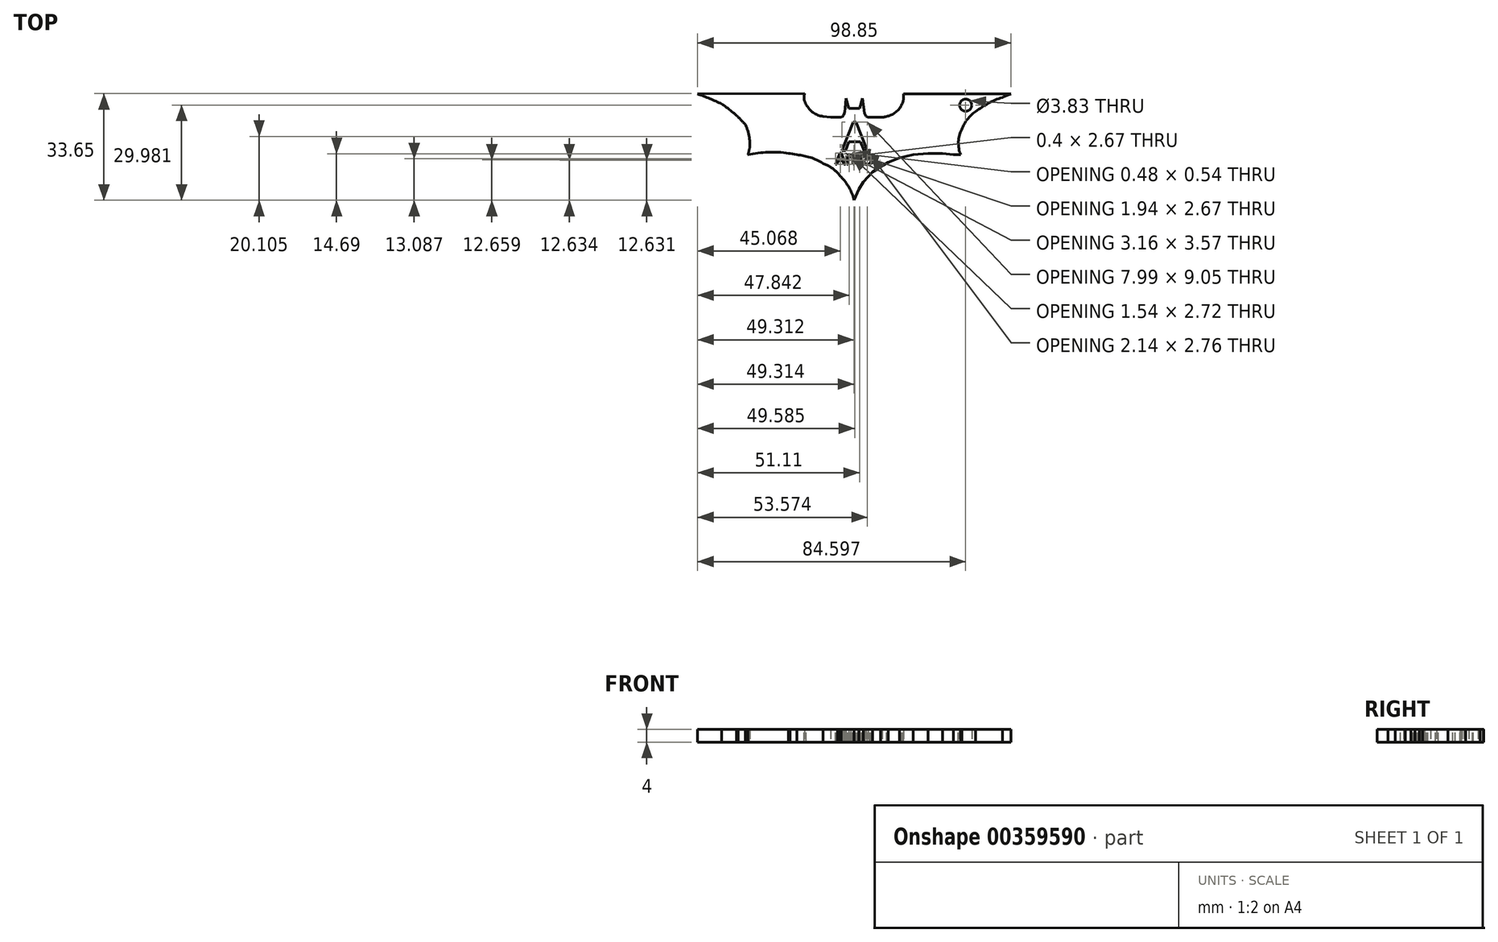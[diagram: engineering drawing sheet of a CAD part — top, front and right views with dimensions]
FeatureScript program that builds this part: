
annotation { "Feature Type Name" : "Feature", "Feature Type Description" : "" }
export const myFeature = defineFeature(function(context is Context, id is Id, definition is map)
    precondition{}
    {
        {
            var Q0;
            Q0=qCreatedBy(makeId("Top.planeOp"),FACE);
            var sketch = newSketch(context, id + "F0", { "sketchPlane" : qUnion([Q0])});
            skLineSegment(sketch, "E0", {"start": v(13.72, 31.25) * mm, "end": v(13.72, 28.83) * mm});
            skLineSegment(sketch, "E1", {"start": v(13.72, 28.83) * mm, "end": v(14.25, 27.77) * mm});
            skLineSegment(sketch, "E2", {"start": v(14.25, 27.77) * mm, "end": v(14.95, 26.82) * mm});
            skLineSegment(sketch, "E3", {"start": v(14.95, 26.82) * mm, "end": v(16.13, 25.57) * mm});
            skLineSegment(sketch, "E4", {"start": v(16.13, 25.57) * mm, "end": v(17.63, 24.91) * mm});
            skLineSegment(sketch, "E5", {"start": v(17.63, 24.91) * mm, "end": v(18.98, 24.45) * mm});
            skLineSegment(sketch, "E6", {"start": v(18.98, 24.45) * mm, "end": v(20.46, 24) * mm});
            skLineSegment(sketch, "E7", {"start": v(20.46, 24) * mm, "end": v(21.96, 23.73) * mm});
            skLineSegment(sketch, "E8", {"start": v(21.96, 23.73) * mm, "end": v(23.63, 23.73) * mm});
            skLineSegment(sketch, "E9", {"start": v(23.63, 23.73) * mm, "end": v(24.39, 23.73) * mm});
            skLineSegment(sketch, "E10", {"start": v(24.39, 23.73) * mm, "end": v(25.19, 23.73) * mm});
            skLineSegment(sketch, "E11", {"start": v(25.19, 23.73) * mm, "end": v(25.75, 24) * mm});
            skLineSegment(sketch, "E12", {"start": v(25.75, 24) * mm, "end": v(26, 24.45) * mm});
            skLineSegment(sketch, "E13", {"start": v(26, 24.45) * mm, "end": v(26.24, 25.03) * mm});
            skLineSegment(sketch, "E14", {"start": v(26.24, 25.03) * mm, "end": v(26.34, 25.57) * mm});
            skLineSegment(sketch, "E15", {"start": v(26.34, 25.57) * mm, "end": v(26.47, 26.55) * mm});
            skLineSegment(sketch, "E16", {"start": v(26.47, 26.55) * mm, "end": v(26.64, 28.28) * mm});
            skLineSegment(sketch, "E17", {"start": v(26.64, 28.28) * mm, "end": v(26.78, 29.75) * mm});
            skLineSegment(sketch, "E18", {"start": v(26.78, 29.75) * mm, "end": v(27.66, 26.55) * mm});
            skLineSegment(sketch, "E19", {"start": v(27.66, 26.55) * mm, "end": v(29.82, 26.55) * mm});
            skLineSegment(sketch, "E20", {"start": v(29.82, 26.55) * mm, "end": v(31.09, 26.55) * mm});
            skLineSegment(sketch, "E21", {"start": v(31.09, 26.55) * mm, "end": v(32.02, 29.75) * mm});
            skLineSegment(sketch, "E22", {"start": v(32.02, 29.75) * mm, "end": v(32.64, 25.03) * mm});
            skLineSegment(sketch, "E23", {"start": v(32.64, 25.03) * mm, "end": v(33.17, 24) * mm});
            skLineSegment(sketch, "E24", {"start": v(33.17, 24) * mm, "end": v(33.75, 23.73) * mm});
            skLineSegment(sketch, "E25", {"start": v(33.75, 23.73) * mm, "end": v(35.1, 23.73) * mm});
            skLineSegment(sketch, "E26", {"start": v(35.1, 23.73) * mm, "end": v(36.67, 23.73) * mm});
            skLineSegment(sketch, "E27", {"start": v(36.67, 23.73) * mm, "end": v(38.2, 23.73) * mm});
            skLineSegment(sketch, "E28", {"start": v(38.2, 23.73) * mm, "end": v(39.59, 24) * mm});
            skLineSegment(sketch, "E29", {"start": v(39.59, 24) * mm, "end": v(41.11, 25.03) * mm});
            skLineSegment(sketch, "E30", {"start": v(41.11, 25.03) * mm, "end": v(42.73, 25.57) * mm});
            skLineSegment(sketch, "E31", {"start": v(42.73, 25.57) * mm, "end": v(43.58, 26.55) * mm});
            skLineSegment(sketch, "E32", {"start": v(43.58, 26.55) * mm, "end": v(44.48, 27.96) * mm});
            skLineSegment(sketch, "E33", {"start": v(44.48, 27.96) * mm, "end": v(44.93, 29.4) * mm});
            skLineSegment(sketch, "E34", {"start": v(44.93, 29.4) * mm, "end": v(44.93, 31.1) * mm});
            skLineSegment(sketch, "E35", {"start": v(44.93, 31.1) * mm, "end": v(78.8, 31.1) * mm});
            skLineSegment(sketch, "E36", {"start": v(78.8, 31.1) * mm, "end": v(73.5, 29.03) * mm});
            skLineSegment(sketch, "E37", {"start": v(73.5, 29.03) * mm, "end": v(70.71, 27.5) * mm});
            skLineSegment(sketch, "E38", {"start": v(70.71, 27.5) * mm, "end": v(67.7, 25.57) * mm});
            skLineSegment(sketch, "E39", {"start": v(67.7, 25.57) * mm, "end": v(65.18, 22.94) * mm});
            skLineSegment(sketch, "E40", {"start": v(65.18, 22.94) * mm, "end": v(64.06, 21.44) * mm});
            skLineSegment(sketch, "E41", {"start": v(64.06, 21.44) * mm, "end": v(63.33, 19.97) * mm});
            skLineSegment(sketch, "E42", {"start": v(63.33, 19.97) * mm, "end": v(62.51, 17.77) * mm});
            skLineSegment(sketch, "E43", {"start": v(62.51, 17.77) * mm, "end": v(62.51, 15.4) * mm});
            skLineSegment(sketch, "E44", {"start": v(62.51, 15.4) * mm, "end": v(63, 11.92) * mm});
            skLineSegment(sketch, "E45", {"start": v(63, 11.92) * mm, "end": v(60.67, 11.92) * mm});
            skLineSegment(sketch, "E46", {"start": v(60.67, 11.92) * mm, "end": v(57.24, 12.33) * mm});
            skLineSegment(sketch, "E47", {"start": v(57.24, 12.33) * mm, "end": v(52.7, 12.33) * mm});
            skLineSegment(sketch, "E48", {"start": v(52.7, 12.33) * mm, "end": v(48.05, 11.92) * mm});
            skLineSegment(sketch, "E49", {"start": v(48.05, 11.92) * mm, "end": v(43.68, 10.94) * mm});
            skLineSegment(sketch, "E50", {"start": v(43.68, 10.94) * mm, "end": v(40.1, 9.5) * mm});
            skLineSegment(sketch, "E51", {"start": v(40.1, 9.5) * mm, "end": v(37.65, 8.21) * mm});
            skLineSegment(sketch, "E52", {"start": v(37.65, 8.21) * mm, "end": v(35.1, 6.52) * mm});
            skLineSegment(sketch, "E53", {"start": v(35.1, 6.52) * mm, "end": v(32.18, 3.37) * mm});
            skLineSegment(sketch, "E54", {"start": v(32.18, 3.37) * mm, "end": v(30.81, 1.1) * mm});
            skLineSegment(sketch, "E55", {"start": v(30.81, 1.1) * mm, "end": v(29.34, -2.4) * mm});
            skLineSegment(sketch, "E56", {"start": v(29.34, -2.4) * mm, "end": v(27.5, 2) * mm});
            skLineSegment(sketch, "E57", {"start": v(27.5, 2) * mm, "end": v(26, 3.93) * mm});
            skLineSegment(sketch, "E58", {"start": v(26, 3.93) * mm, "end": v(24.39, 6.05) * mm});
            skLineSegment(sketch, "E59", {"start": v(24.39, 6.05) * mm, "end": v(22.41, 7.44) * mm});
            skLineSegment(sketch, "E60", {"start": v(22.41, 7.44) * mm, "end": v(20.46, 8.75) * mm});
            skLineSegment(sketch, "E61", {"start": v(20.46, 8.75) * mm, "end": v(17.41, 10.24) * mm});
            skLineSegment(sketch, "E62", {"start": v(17.41, 10.24) * mm, "end": v(14.24, 11.29) * mm});
            skLineSegment(sketch, "E63", {"start": v(14.24, 11.29) * mm, "end": v(11.29, 11.92) * mm});
            skLineSegment(sketch, "E64", {"start": v(11.29, 11.92) * mm, "end": v(9.12, 12.4) * mm});
            skLineSegment(sketch, "E65", {"start": v(9.12, 12.4) * mm, "end": v(5.3, 12.4) * mm});
            skLineSegment(sketch, "E66", {"start": v(5.3, 12.4) * mm, "end": v(2.38, 12.4) * mm});
            skLineSegment(sketch, "E67", {"start": v(2.38, 12.4) * mm, "end": v(-0.95, 12.4) * mm});
            skLineSegment(sketch, "E68", {"start": v(-0.95, 12.4) * mm, "end": v(-4.16, 11.92) * mm});
            skLineSegment(sketch, "E69", {"start": v(-4.16, 11.92) * mm, "end": v(-3.57, 14.45) * mm});
            skLineSegment(sketch, "E70", {"start": v(-3.57, 14.45) * mm, "end": v(-3.57, 16.43) * mm});
            skLineSegment(sketch, "E71", {"start": v(-3.57, 16.43) * mm, "end": v(-4.05, 19) * mm});
            skLineSegment(sketch, "E72", {"start": v(-4.05, 19) * mm, "end": v(-5, 21.44) * mm});
            skLineSegment(sketch, "E73", {"start": v(-5, 21.44) * mm, "end": v(-6.4, 22.94) * mm});
            skLineSegment(sketch, "E74", {"start": v(-6.4, 22.94) * mm, "end": v(-7.45, 24) * mm});
            skLineSegment(sketch, "E75", {"start": v(-7.45, 24) * mm, "end": v(-9.22, 25.57) * mm});
            skLineSegment(sketch, "E76", {"start": v(-9.22, 25.57) * mm, "end": v(-10.64, 26.55) * mm});
            skLineSegment(sketch, "E77", {"start": v(-10.64, 26.55) * mm, "end": v(-12.42, 27.96) * mm});
            skLineSegment(sketch, "E78", {"start": v(-12.42, 27.96) * mm, "end": v(-15.57, 29.4) * mm});
            skLineSegment(sketch, "E79", {"start": v(-15.57, 29.4) * mm, "end": v(-20.04, 31.1) * mm});
            skLineSegment(sketch, "E80", {"start": v(-20.04, 31.1) * mm, "end": v(13.72, 31.25) * mm});
            skSolve(sketch);
        }
        {
            var Q0;
            Q0 = qSketchRegion(id + "F0", true);
            extrude(context, id + "F1", {"entities" : qUnion([Q0]), "depth" : 4 * mm});
        }
        {
            var Q0;
            Q0=makeQuery(id+"F1.opExtrude","CAP_FACE",FACE,{"disambiguationData":[OSD([sQuery(id+"F0.wireOp",EDGE,"E0"),sQuery(id+"F0.wireOp",EDGE,"E1"),sQuery(id+"F0.wireOp",EDGE,"E2"),sQuery(id+"F0.wireOp",EDGE,"E3"),sQuery(id+"F0.wireOp",EDGE,"E4"),sQuery(id+"F0.wireOp",EDGE,"E5"),sQuery(id+"F0.wireOp",EDGE,"E6"),sQuery(id+"F0.wireOp",EDGE,"E7"),sQuery(id+"F0.wireOp",EDGE,"E8"),sQuery(id+"F0.wireOp",EDGE,"E9"),sQuery(id+"F0.wireOp",EDGE,"E10"),sQuery(id+"F0.wireOp",EDGE,"E11"),sQuery(id+"F0.wireOp",EDGE,"E12"),sQuery(id+"F0.wireOp",EDGE,"E13"),sQuery(id+"F0.wireOp",EDGE,"E14"),sQuery(id+"F0.wireOp",EDGE,"E15"),sQuery(id+"F0.wireOp",EDGE,"E16"),sQuery(id+"F0.wireOp",EDGE,"E17"),sQuery(id+"F0.wireOp",EDGE,"E18"),sQuery(id+"F0.wireOp",EDGE,"E19"),sQuery(id+"F0.wireOp",EDGE,"E20"),sQuery(id+"F0.wireOp",EDGE,"E21"),sQuery(id+"F0.wireOp",EDGE,"E22"),sQuery(id+"F0.wireOp",EDGE,"E23"),sQuery(id+"F0.wireOp",EDGE,"E24"),sQuery(id+"F0.wireOp",EDGE,"E25"),sQuery(id+"F0.wireOp",EDGE,"E26"),sQuery(id+"F0.wireOp",EDGE,"E27"),sQuery(id+"F0.wireOp",EDGE,"E28"),sQuery(id+"F0.wireOp",EDGE,"E29"),sQuery(id+"F0.wireOp",EDGE,"E30"),sQuery(id+"F0.wireOp",EDGE,"E31"),sQuery(id+"F0.wireOp",EDGE,"E32"),sQuery(id+"F0.wireOp",EDGE,"E33"),sQuery(id+"F0.wireOp",EDGE,"E34"),sQuery(id+"F0.wireOp",EDGE,"E35"),sQuery(id+"F0.wireOp",EDGE,"E36"),sQuery(id+"F0.wireOp",EDGE,"E37"),sQuery(id+"F0.wireOp",EDGE,"E38"),sQuery(id+"F0.wireOp",EDGE,"E39"),sQuery(id+"F0.wireOp",EDGE,"E40"),sQuery(id+"F0.wireOp",EDGE,"E41"),sQuery(id+"F0.wireOp",EDGE,"E42"),sQuery(id+"F0.wireOp",EDGE,"E43"),sQuery(id+"F0.wireOp",EDGE,"E44"),sQuery(id+"F0.wireOp",EDGE,"E45"),sQuery(id+"F0.wireOp",EDGE,"E46"),sQuery(id+"F0.wireOp",EDGE,"E47"),sQuery(id+"F0.wireOp",EDGE,"E48"),sQuery(id+"F0.wireOp",EDGE,"E49"),sQuery(id+"F0.wireOp",EDGE,"E50"),sQuery(id+"F0.wireOp",EDGE,"E51"),sQuery(id+"F0.wireOp",EDGE,"E52"),sQuery(id+"F0.wireOp",EDGE,"E53"),sQuery(id+"F0.wireOp",EDGE,"E54"),sQuery(id+"F0.wireOp",EDGE,"E55"),sQuery(id+"F0.wireOp",EDGE,"E56"),sQuery(id+"F0.wireOp",EDGE,"E57"),sQuery(id+"F0.wireOp",EDGE,"E58"),sQuery(id+"F0.wireOp",EDGE,"E59"),sQuery(id+"F0.wireOp",EDGE,"E60"),sQuery(id+"F0.wireOp",EDGE,"E61"),sQuery(id+"F0.wireOp",EDGE,"E62"),sQuery(id+"F0.wireOp",EDGE,"E63"),sQuery(id+"F0.wireOp",EDGE,"E64"),sQuery(id+"F0.wireOp",EDGE,"E65"),sQuery(id+"F0.wireOp",EDGE,"E66"),sQuery(id+"F0.wireOp",EDGE,"E67"),sQuery(id+"F0.wireOp",EDGE,"E68"),sQuery(id+"F0.wireOp",EDGE,"E69"),sQuery(id+"F0.wireOp",EDGE,"E70"),sQuery(id+"F0.wireOp",EDGE,"E71"),sQuery(id+"F0.wireOp",EDGE,"E72"),sQuery(id+"F0.wireOp",EDGE,"E73"),sQuery(id+"F0.wireOp",EDGE,"E74"),sQuery(id+"F0.wireOp",EDGE,"E75"),sQuery(id+"F0.wireOp",EDGE,"E76"),sQuery(id+"F0.wireOp",EDGE,"E77"),sQuery(id+"F0.wireOp",EDGE,"E78"),sQuery(id+"F0.wireOp",EDGE,"E79"),sQuery(id+"F0.wireOp",EDGE,"E80")])],"isStart":false});
            var sketch = newSketch(context, id + "F2", { "sketchPlane" : qUnion([Q0])});
            skArc(sketch, "E81", {"start": v(44.48, 27.96) * mm, "mid": v(44.94, 29.5) * mm, "end": v(44.93, 31.1) * mm});
            skArc(sketch, "E82", {"start": v(39.59, 24) * mm, "mid": v(42.52, 25.38) * mm, "end": v(44.48, 27.96) * mm});
            skArc(sketch, "E83", {"start": v(38.2, 23.73) * mm, "mid": v(38.9, 23.86) * mm, "end": v(39.59, 24) * mm});
            skLineSegment(sketch, "E84", {"start": v(38.2, 23.73) * mm, "end": v(44.93, 31.1) * mm});
            skSolve(sketch);
        }
        {
            var Q0;
            Q0 = qSketchRegion(id + "F2", true);
            extrude(context, id + "F3", {"entities" : qUnion([Q0]), "operationType" : NewBodyOperationType.REMOVE, "oppositeDirection" : true, "depth" : 25 * mm});
        }
        {
            var Q0;
            Q0=makeQuery(id+"F1.opExtrude","CAP_FACE",FACE,{"disambiguationData":[OSD([sQuery(id+"F0.wireOp",EDGE,"E0"),sQuery(id+"F0.wireOp",EDGE,"E1"),sQuery(id+"F0.wireOp",EDGE,"E2"),sQuery(id+"F0.wireOp",EDGE,"E3"),sQuery(id+"F0.wireOp",EDGE,"E4"),sQuery(id+"F0.wireOp",EDGE,"E5"),sQuery(id+"F0.wireOp",EDGE,"E6"),sQuery(id+"F0.wireOp",EDGE,"E7"),sQuery(id+"F0.wireOp",EDGE,"E8"),sQuery(id+"F0.wireOp",EDGE,"E9"),sQuery(id+"F0.wireOp",EDGE,"E10"),sQuery(id+"F0.wireOp",EDGE,"E11"),sQuery(id+"F0.wireOp",EDGE,"E12"),sQuery(id+"F0.wireOp",EDGE,"E13"),sQuery(id+"F0.wireOp",EDGE,"E14"),sQuery(id+"F0.wireOp",EDGE,"E15"),sQuery(id+"F0.wireOp",EDGE,"E16"),sQuery(id+"F0.wireOp",EDGE,"E17"),sQuery(id+"F0.wireOp",EDGE,"E18"),sQuery(id+"F0.wireOp",EDGE,"E19"),sQuery(id+"F0.wireOp",EDGE,"E20"),sQuery(id+"F0.wireOp",EDGE,"E21"),sQuery(id+"F0.wireOp",EDGE,"E22"),sQuery(id+"F0.wireOp",EDGE,"E23"),sQuery(id+"F0.wireOp",EDGE,"E24"),sQuery(id+"F0.wireOp",EDGE,"E25"),sQuery(id+"F0.wireOp",EDGE,"E26"),sQuery(id+"F0.wireOp",EDGE,"E27"),sQuery(id+"F0.wireOp",EDGE,"E28"),sQuery(id+"F0.wireOp",EDGE,"E29"),sQuery(id+"F0.wireOp",EDGE,"E30"),sQuery(id+"F0.wireOp",EDGE,"E31"),sQuery(id+"F0.wireOp",EDGE,"E32"),sQuery(id+"F0.wireOp",EDGE,"E33"),sQuery(id+"F0.wireOp",EDGE,"E34"),sQuery(id+"F0.wireOp",EDGE,"E35"),sQuery(id+"F0.wireOp",EDGE,"E36"),sQuery(id+"F0.wireOp",EDGE,"E37"),sQuery(id+"F0.wireOp",EDGE,"E38"),sQuery(id+"F0.wireOp",EDGE,"E39"),sQuery(id+"F0.wireOp",EDGE,"E40"),sQuery(id+"F0.wireOp",EDGE,"E41"),sQuery(id+"F0.wireOp",EDGE,"E42"),sQuery(id+"F0.wireOp",EDGE,"E43"),sQuery(id+"F0.wireOp",EDGE,"E44"),sQuery(id+"F0.wireOp",EDGE,"E45"),sQuery(id+"F0.wireOp",EDGE,"E46"),sQuery(id+"F0.wireOp",EDGE,"E47"),sQuery(id+"F0.wireOp",EDGE,"E48"),sQuery(id+"F0.wireOp",EDGE,"E49"),sQuery(id+"F0.wireOp",EDGE,"E50"),sQuery(id+"F0.wireOp",EDGE,"E51"),sQuery(id+"F0.wireOp",EDGE,"E52"),sQuery(id+"F0.wireOp",EDGE,"E53"),sQuery(id+"F0.wireOp",EDGE,"E54"),sQuery(id+"F0.wireOp",EDGE,"E55"),sQuery(id+"F0.wireOp",EDGE,"E56"),sQuery(id+"F0.wireOp",EDGE,"E57"),sQuery(id+"F0.wireOp",EDGE,"E58"),sQuery(id+"F0.wireOp",EDGE,"E59"),sQuery(id+"F0.wireOp",EDGE,"E60"),sQuery(id+"F0.wireOp",EDGE,"E61"),sQuery(id+"F0.wireOp",EDGE,"E62"),sQuery(id+"F0.wireOp",EDGE,"E63"),sQuery(id+"F0.wireOp",EDGE,"E64"),sQuery(id+"F0.wireOp",EDGE,"E65"),sQuery(id+"F0.wireOp",EDGE,"E66"),sQuery(id+"F0.wireOp",EDGE,"E67"),sQuery(id+"F0.wireOp",EDGE,"E68"),sQuery(id+"F0.wireOp",EDGE,"E69"),sQuery(id+"F0.wireOp",EDGE,"E70"),sQuery(id+"F0.wireOp",EDGE,"E71"),sQuery(id+"F0.wireOp",EDGE,"E72"),sQuery(id+"F0.wireOp",EDGE,"E73"),sQuery(id+"F0.wireOp",EDGE,"E74"),sQuery(id+"F0.wireOp",EDGE,"E75"),sQuery(id+"F0.wireOp",EDGE,"E76"),sQuery(id+"F0.wireOp",EDGE,"E77"),sQuery(id+"F0.wireOp",EDGE,"E78"),sQuery(id+"F0.wireOp",EDGE,"E79"),sQuery(id+"F0.wireOp",EDGE,"E80")])],"isStart":false});
            var sketch = newSketch(context, id + "F4", { "sketchPlane" : qUnion([Q0])});
            skArc(sketch, "E85", {"start": v(13.72, 31.25) * mm, "mid": v(13.57, 29.44) * mm, "end": v(14.25, 27.77) * mm});
            skArc(sketch, "E86", {"start": v(14.25, 27.77) * mm, "mid": v(16.81, 24.99) * mm, "end": v(20.46, 24) * mm});
            skLineSegment(sketch, "E87", {"start": v(20.46, 24) * mm, "end": v(13.72, 31.25) * mm});
            skSolve(sketch);
        }
        {
            var Q0;
            Q0 = qSketchRegion(id + "F4", true);
            extrude(context, id + "F5", {"entities" : qUnion([Q0]), "operationType" : NewBodyOperationType.REMOVE, "oppositeDirection" : true, "depth" : 25 * mm});
        }
        {
            var Q0;
            Q0=makeQuery(id+"F1.opExtrude","CAP_FACE",FACE,{"disambiguationData":[OSD([sQuery(id+"F0.wireOp",EDGE,"E0"),sQuery(id+"F0.wireOp",EDGE,"E1"),sQuery(id+"F0.wireOp",EDGE,"E2"),sQuery(id+"F0.wireOp",EDGE,"E3"),sQuery(id+"F0.wireOp",EDGE,"E4"),sQuery(id+"F0.wireOp",EDGE,"E5"),sQuery(id+"F0.wireOp",EDGE,"E6"),sQuery(id+"F0.wireOp",EDGE,"E7"),sQuery(id+"F0.wireOp",EDGE,"E8"),sQuery(id+"F0.wireOp",EDGE,"E9"),sQuery(id+"F0.wireOp",EDGE,"E10"),sQuery(id+"F0.wireOp",EDGE,"E11"),sQuery(id+"F0.wireOp",EDGE,"E12"),sQuery(id+"F0.wireOp",EDGE,"E13"),sQuery(id+"F0.wireOp",EDGE,"E14"),sQuery(id+"F0.wireOp",EDGE,"E15"),sQuery(id+"F0.wireOp",EDGE,"E16"),sQuery(id+"F0.wireOp",EDGE,"E17"),sQuery(id+"F0.wireOp",EDGE,"E18"),sQuery(id+"F0.wireOp",EDGE,"E19"),sQuery(id+"F0.wireOp",EDGE,"E20"),sQuery(id+"F0.wireOp",EDGE,"E21"),sQuery(id+"F0.wireOp",EDGE,"E22"),sQuery(id+"F0.wireOp",EDGE,"E23"),sQuery(id+"F0.wireOp",EDGE,"E24"),sQuery(id+"F0.wireOp",EDGE,"E25"),sQuery(id+"F0.wireOp",EDGE,"E26"),sQuery(id+"F0.wireOp",EDGE,"E27"),sQuery(id+"F0.wireOp",EDGE,"E28"),sQuery(id+"F0.wireOp",EDGE,"E29"),sQuery(id+"F0.wireOp",EDGE,"E30"),sQuery(id+"F0.wireOp",EDGE,"E31"),sQuery(id+"F0.wireOp",EDGE,"E32"),sQuery(id+"F0.wireOp",EDGE,"E33"),sQuery(id+"F0.wireOp",EDGE,"E34"),sQuery(id+"F0.wireOp",EDGE,"E35"),sQuery(id+"F0.wireOp",EDGE,"E36"),sQuery(id+"F0.wireOp",EDGE,"E37"),sQuery(id+"F0.wireOp",EDGE,"E38"),sQuery(id+"F0.wireOp",EDGE,"E39"),sQuery(id+"F0.wireOp",EDGE,"E40"),sQuery(id+"F0.wireOp",EDGE,"E41"),sQuery(id+"F0.wireOp",EDGE,"E42"),sQuery(id+"F0.wireOp",EDGE,"E43"),sQuery(id+"F0.wireOp",EDGE,"E44"),sQuery(id+"F0.wireOp",EDGE,"E45"),sQuery(id+"F0.wireOp",EDGE,"E46"),sQuery(id+"F0.wireOp",EDGE,"E47"),sQuery(id+"F0.wireOp",EDGE,"E48"),sQuery(id+"F0.wireOp",EDGE,"E49"),sQuery(id+"F0.wireOp",EDGE,"E50"),sQuery(id+"F0.wireOp",EDGE,"E51"),sQuery(id+"F0.wireOp",EDGE,"E52"),sQuery(id+"F0.wireOp",EDGE,"E53"),sQuery(id+"F0.wireOp",EDGE,"E54"),sQuery(id+"F0.wireOp",EDGE,"E55"),sQuery(id+"F0.wireOp",EDGE,"E56"),sQuery(id+"F0.wireOp",EDGE,"E57"),sQuery(id+"F0.wireOp",EDGE,"E58"),sQuery(id+"F0.wireOp",EDGE,"E59"),sQuery(id+"F0.wireOp",EDGE,"E60"),sQuery(id+"F0.wireOp",EDGE,"E61"),sQuery(id+"F0.wireOp",EDGE,"E62"),sQuery(id+"F0.wireOp",EDGE,"E63"),sQuery(id+"F0.wireOp",EDGE,"E64"),sQuery(id+"F0.wireOp",EDGE,"E65"),sQuery(id+"F0.wireOp",EDGE,"E66"),sQuery(id+"F0.wireOp",EDGE,"E67"),sQuery(id+"F0.wireOp",EDGE,"E68"),sQuery(id+"F0.wireOp",EDGE,"E69"),sQuery(id+"F0.wireOp",EDGE,"E70"),sQuery(id+"F0.wireOp",EDGE,"E71"),sQuery(id+"F0.wireOp",EDGE,"E72"),sQuery(id+"F0.wireOp",EDGE,"E73"),sQuery(id+"F0.wireOp",EDGE,"E74"),sQuery(id+"F0.wireOp",EDGE,"E75"),sQuery(id+"F0.wireOp",EDGE,"E76"),sQuery(id+"F0.wireOp",EDGE,"E77"),sQuery(id+"F0.wireOp",EDGE,"E78"),sQuery(id+"F0.wireOp",EDGE,"E79"),sQuery(id+"F0.wireOp",EDGE,"E80")])],"isStart":false});
            var sketch = newSketch(context, id + "F6", { "sketchPlane" : qUnion([Q0])});
            skLineSegment(sketch, "E88", {"start": v(19.36, 24.08) * mm, "end": v(21.96, 23.73) * mm});
            skLineSegment(sketch, "E89", {"start": v(21.96, 23.73) * mm, "end": v(21.96, 24.89) * mm});
            skLineSegment(sketch, "E90", {"start": v(21.96, 24.89) * mm, "end": v(19.54, 24.89) * mm});
            skLineSegment(sketch, "E91", {"start": v(19.54, 24.89) * mm, "end": v(19.36, 24.08) * mm});
            skSolve(sketch);
        }
        {
            var Q0;
            Q0 = qSketchRegion(id + "F6", true);
            extrude(context, id + "F7", {"entities" : qUnion([Q0]), "operationType" : NewBodyOperationType.REMOVE, "oppositeDirection" : true, "depth" : 25 * mm});
        }
        {
            var Q0;
            Q0=makeQuery(id+"F1.opExtrude","CAP_FACE",FACE,{"disambiguationData":[OSD([sQuery(id+"F0.wireOp",EDGE,"E0"),sQuery(id+"F0.wireOp",EDGE,"E1"),sQuery(id+"F0.wireOp",EDGE,"E2"),sQuery(id+"F0.wireOp",EDGE,"E3"),sQuery(id+"F0.wireOp",EDGE,"E4"),sQuery(id+"F0.wireOp",EDGE,"E5"),sQuery(id+"F0.wireOp",EDGE,"E6"),sQuery(id+"F0.wireOp",EDGE,"E7"),sQuery(id+"F0.wireOp",EDGE,"E8"),sQuery(id+"F0.wireOp",EDGE,"E9"),sQuery(id+"F0.wireOp",EDGE,"E10"),sQuery(id+"F0.wireOp",EDGE,"E11"),sQuery(id+"F0.wireOp",EDGE,"E12"),sQuery(id+"F0.wireOp",EDGE,"E13"),sQuery(id+"F0.wireOp",EDGE,"E14"),sQuery(id+"F0.wireOp",EDGE,"E15"),sQuery(id+"F0.wireOp",EDGE,"E16"),sQuery(id+"F0.wireOp",EDGE,"E17"),sQuery(id+"F0.wireOp",EDGE,"E18"),sQuery(id+"F0.wireOp",EDGE,"E19"),sQuery(id+"F0.wireOp",EDGE,"E20"),sQuery(id+"F0.wireOp",EDGE,"E21"),sQuery(id+"F0.wireOp",EDGE,"E22"),sQuery(id+"F0.wireOp",EDGE,"E23"),sQuery(id+"F0.wireOp",EDGE,"E24"),sQuery(id+"F0.wireOp",EDGE,"E25"),sQuery(id+"F0.wireOp",EDGE,"E26"),sQuery(id+"F0.wireOp",EDGE,"E27"),sQuery(id+"F0.wireOp",EDGE,"E28"),sQuery(id+"F0.wireOp",EDGE,"E29"),sQuery(id+"F0.wireOp",EDGE,"E30"),sQuery(id+"F0.wireOp",EDGE,"E31"),sQuery(id+"F0.wireOp",EDGE,"E32"),sQuery(id+"F0.wireOp",EDGE,"E33"),sQuery(id+"F0.wireOp",EDGE,"E34"),sQuery(id+"F0.wireOp",EDGE,"E35"),sQuery(id+"F0.wireOp",EDGE,"E36"),sQuery(id+"F0.wireOp",EDGE,"E37"),sQuery(id+"F0.wireOp",EDGE,"E38"),sQuery(id+"F0.wireOp",EDGE,"E39"),sQuery(id+"F0.wireOp",EDGE,"E40"),sQuery(id+"F0.wireOp",EDGE,"E41"),sQuery(id+"F0.wireOp",EDGE,"E42"),sQuery(id+"F0.wireOp",EDGE,"E43"),sQuery(id+"F0.wireOp",EDGE,"E44"),sQuery(id+"F0.wireOp",EDGE,"E45"),sQuery(id+"F0.wireOp",EDGE,"E46"),sQuery(id+"F0.wireOp",EDGE,"E47"),sQuery(id+"F0.wireOp",EDGE,"E48"),sQuery(id+"F0.wireOp",EDGE,"E49"),sQuery(id+"F0.wireOp",EDGE,"E50"),sQuery(id+"F0.wireOp",EDGE,"E51"),sQuery(id+"F0.wireOp",EDGE,"E52"),sQuery(id+"F0.wireOp",EDGE,"E53"),sQuery(id+"F0.wireOp",EDGE,"E54"),sQuery(id+"F0.wireOp",EDGE,"E55"),sQuery(id+"F0.wireOp",EDGE,"E56"),sQuery(id+"F0.wireOp",EDGE,"E57"),sQuery(id+"F0.wireOp",EDGE,"E58"),sQuery(id+"F0.wireOp",EDGE,"E59"),sQuery(id+"F0.wireOp",EDGE,"E60"),sQuery(id+"F0.wireOp",EDGE,"E61"),sQuery(id+"F0.wireOp",EDGE,"E62"),sQuery(id+"F0.wireOp",EDGE,"E63"),sQuery(id+"F0.wireOp",EDGE,"E64"),sQuery(id+"F0.wireOp",EDGE,"E65"),sQuery(id+"F0.wireOp",EDGE,"E66"),sQuery(id+"F0.wireOp",EDGE,"E67"),sQuery(id+"F0.wireOp",EDGE,"E68"),sQuery(id+"F0.wireOp",EDGE,"E69"),sQuery(id+"F0.wireOp",EDGE,"E70"),sQuery(id+"F0.wireOp",EDGE,"E71"),sQuery(id+"F0.wireOp",EDGE,"E72"),sQuery(id+"F0.wireOp",EDGE,"E73"),sQuery(id+"F0.wireOp",EDGE,"E74"),sQuery(id+"F0.wireOp",EDGE,"E75"),sQuery(id+"F0.wireOp",EDGE,"E76"),sQuery(id+"F0.wireOp",EDGE,"E77"),sQuery(id+"F0.wireOp",EDGE,"E78"),sQuery(id+"F0.wireOp",EDGE,"E79"),sQuery(id+"F0.wireOp",EDGE,"E80")])],"isStart":false});
            var sketch = newSketch(context, id + "F8", { "sketchPlane" : qUnion([Q0])});
            skArc(sketch, "E92", {"start": v(-4.16, 11.92) * mm, "mid": v(-3.65, 16.77) * mm, "end": v(-5, 21.44) * mm});
            skArc(sketch, "E93", {"start": v(-5, 21.44) * mm, "mid": v(-8.5, 24.95) * mm, "end": v(-12.42, 27.96) * mm});
            skArc(sketch, "E94", {"start": v(-12.42, 27.96) * mm, "mid": v(-16.18, 29.65) * mm, "end": v(-20.04, 31.1) * mm});
            skLineSegment(sketch, "E95", {"start": v(-20.04, 31.1) * mm, "end": v(-4.16, 11.92) * mm});
            skSolve(sketch);
        }
        {
            var Q0;
            Q0 = qSketchRegion(id + "F8", true);
            extrude(context, id + "F9", {"entities" : qUnion([Q0]), "operationType" : NewBodyOperationType.REMOVE, "oppositeDirection" : true, "depth" : 25 * mm});
        }
        {
            var Q0;
            Q0=makeQuery(id+"F1.opExtrude","CAP_FACE",FACE,{"disambiguationData":[OSD([sQuery(id+"F0.wireOp",EDGE,"E0"),sQuery(id+"F0.wireOp",EDGE,"E1"),sQuery(id+"F0.wireOp",EDGE,"E2"),sQuery(id+"F0.wireOp",EDGE,"E3"),sQuery(id+"F0.wireOp",EDGE,"E4"),sQuery(id+"F0.wireOp",EDGE,"E5"),sQuery(id+"F0.wireOp",EDGE,"E6"),sQuery(id+"F0.wireOp",EDGE,"E7"),sQuery(id+"F0.wireOp",EDGE,"E8"),sQuery(id+"F0.wireOp",EDGE,"E9"),sQuery(id+"F0.wireOp",EDGE,"E10"),sQuery(id+"F0.wireOp",EDGE,"E11"),sQuery(id+"F0.wireOp",EDGE,"E12"),sQuery(id+"F0.wireOp",EDGE,"E13"),sQuery(id+"F0.wireOp",EDGE,"E14"),sQuery(id+"F0.wireOp",EDGE,"E15"),sQuery(id+"F0.wireOp",EDGE,"E16"),sQuery(id+"F0.wireOp",EDGE,"E17"),sQuery(id+"F0.wireOp",EDGE,"E18"),sQuery(id+"F0.wireOp",EDGE,"E19"),sQuery(id+"F0.wireOp",EDGE,"E20"),sQuery(id+"F0.wireOp",EDGE,"E21"),sQuery(id+"F0.wireOp",EDGE,"E22"),sQuery(id+"F0.wireOp",EDGE,"E23"),sQuery(id+"F0.wireOp",EDGE,"E24"),sQuery(id+"F0.wireOp",EDGE,"E25"),sQuery(id+"F0.wireOp",EDGE,"E26"),sQuery(id+"F0.wireOp",EDGE,"E27"),sQuery(id+"F0.wireOp",EDGE,"E28"),sQuery(id+"F0.wireOp",EDGE,"E29"),sQuery(id+"F0.wireOp",EDGE,"E30"),sQuery(id+"F0.wireOp",EDGE,"E31"),sQuery(id+"F0.wireOp",EDGE,"E32"),sQuery(id+"F0.wireOp",EDGE,"E33"),sQuery(id+"F0.wireOp",EDGE,"E34"),sQuery(id+"F0.wireOp",EDGE,"E35"),sQuery(id+"F0.wireOp",EDGE,"E36"),sQuery(id+"F0.wireOp",EDGE,"E37"),sQuery(id+"F0.wireOp",EDGE,"E38"),sQuery(id+"F0.wireOp",EDGE,"E39"),sQuery(id+"F0.wireOp",EDGE,"E40"),sQuery(id+"F0.wireOp",EDGE,"E41"),sQuery(id+"F0.wireOp",EDGE,"E42"),sQuery(id+"F0.wireOp",EDGE,"E43"),sQuery(id+"F0.wireOp",EDGE,"E44"),sQuery(id+"F0.wireOp",EDGE,"E45"),sQuery(id+"F0.wireOp",EDGE,"E46"),sQuery(id+"F0.wireOp",EDGE,"E47"),sQuery(id+"F0.wireOp",EDGE,"E48"),sQuery(id+"F0.wireOp",EDGE,"E49"),sQuery(id+"F0.wireOp",EDGE,"E50"),sQuery(id+"F0.wireOp",EDGE,"E51"),sQuery(id+"F0.wireOp",EDGE,"E52"),sQuery(id+"F0.wireOp",EDGE,"E53"),sQuery(id+"F0.wireOp",EDGE,"E54"),sQuery(id+"F0.wireOp",EDGE,"E55"),sQuery(id+"F0.wireOp",EDGE,"E56"),sQuery(id+"F0.wireOp",EDGE,"E57"),sQuery(id+"F0.wireOp",EDGE,"E58"),sQuery(id+"F0.wireOp",EDGE,"E59"),sQuery(id+"F0.wireOp",EDGE,"E60"),sQuery(id+"F0.wireOp",EDGE,"E61"),sQuery(id+"F0.wireOp",EDGE,"E62"),sQuery(id+"F0.wireOp",EDGE,"E63"),sQuery(id+"F0.wireOp",EDGE,"E64"),sQuery(id+"F0.wireOp",EDGE,"E65"),sQuery(id+"F0.wireOp",EDGE,"E66"),sQuery(id+"F0.wireOp",EDGE,"E67"),sQuery(id+"F0.wireOp",EDGE,"E68"),sQuery(id+"F0.wireOp",EDGE,"E69"),sQuery(id+"F0.wireOp",EDGE,"E70"),sQuery(id+"F0.wireOp",EDGE,"E71"),sQuery(id+"F0.wireOp",EDGE,"E72"),sQuery(id+"F0.wireOp",EDGE,"E73"),sQuery(id+"F0.wireOp",EDGE,"E74"),sQuery(id+"F0.wireOp",EDGE,"E75"),sQuery(id+"F0.wireOp",EDGE,"E76"),sQuery(id+"F0.wireOp",EDGE,"E77"),sQuery(id+"F0.wireOp",EDGE,"E78"),sQuery(id+"F0.wireOp",EDGE,"E79"),sQuery(id+"F0.wireOp",EDGE,"E80")])],"isStart":false});
            var sketch = newSketch(context, id + "F10", { "sketchPlane" : qUnion([Q0])});
            skArc(sketch, "E96", {"start": v(63.33, 19.97) * mm, "mid": v(62.27, 15.99) * mm, "end": v(63, 11.92) * mm});
            skArc(sketch, "E97", {"start": v(67.7, 25.57) * mm, "mid": v(65.08, 23.11) * mm, "end": v(63.33, 19.97) * mm});
            skArc(sketch, "E98", {"start": v(76.15, 30.07) * mm, "mid": v(71.74, 28.17) * mm, "end": v(67.7, 25.57) * mm});
            skArc(sketch, "E99", {"start": v(78.8, 31.1) * mm, "mid": v(77.47, 30.6) * mm, "end": v(76.15, 30.07) * mm});
            skLineSegment(sketch, "E100", {"start": v(78.8, 31.1) * mm, "end": v(63, 11.92) * mm});
            skSolve(sketch);
        }
        {
            var Q0;
            Q0 = qSketchRegion(id + "F10", true);
            extrude(context, id + "F11", {"entities" : qUnion([Q0]), "operationType" : NewBodyOperationType.REMOVE, "oppositeDirection" : true, "depth" : 25 * mm});
        }
        {
            var Q0;
            Q0=makeQuery(id+"F1.opExtrude","CAP_FACE",FACE,{"disambiguationData":[OSD([sQuery(id+"F0.wireOp",EDGE,"E0"),sQuery(id+"F0.wireOp",EDGE,"E1"),sQuery(id+"F0.wireOp",EDGE,"E2"),sQuery(id+"F0.wireOp",EDGE,"E3"),sQuery(id+"F0.wireOp",EDGE,"E4"),sQuery(id+"F0.wireOp",EDGE,"E5"),sQuery(id+"F0.wireOp",EDGE,"E6"),sQuery(id+"F0.wireOp",EDGE,"E7"),sQuery(id+"F0.wireOp",EDGE,"E8"),sQuery(id+"F0.wireOp",EDGE,"E9"),sQuery(id+"F0.wireOp",EDGE,"E10"),sQuery(id+"F0.wireOp",EDGE,"E11"),sQuery(id+"F0.wireOp",EDGE,"E12"),sQuery(id+"F0.wireOp",EDGE,"E13"),sQuery(id+"F0.wireOp",EDGE,"E14"),sQuery(id+"F0.wireOp",EDGE,"E15"),sQuery(id+"F0.wireOp",EDGE,"E16"),sQuery(id+"F0.wireOp",EDGE,"E17"),sQuery(id+"F0.wireOp",EDGE,"E18"),sQuery(id+"F0.wireOp",EDGE,"E19"),sQuery(id+"F0.wireOp",EDGE,"E20"),sQuery(id+"F0.wireOp",EDGE,"E21"),sQuery(id+"F0.wireOp",EDGE,"E22"),sQuery(id+"F0.wireOp",EDGE,"E23"),sQuery(id+"F0.wireOp",EDGE,"E24"),sQuery(id+"F0.wireOp",EDGE,"E25"),sQuery(id+"F0.wireOp",EDGE,"E26"),sQuery(id+"F0.wireOp",EDGE,"E27"),sQuery(id+"F0.wireOp",EDGE,"E28"),sQuery(id+"F0.wireOp",EDGE,"E29"),sQuery(id+"F0.wireOp",EDGE,"E30"),sQuery(id+"F0.wireOp",EDGE,"E31"),sQuery(id+"F0.wireOp",EDGE,"E32"),sQuery(id+"F0.wireOp",EDGE,"E33"),sQuery(id+"F0.wireOp",EDGE,"E34"),sQuery(id+"F0.wireOp",EDGE,"E35"),sQuery(id+"F0.wireOp",EDGE,"E36"),sQuery(id+"F0.wireOp",EDGE,"E37"),sQuery(id+"F0.wireOp",EDGE,"E38"),sQuery(id+"F0.wireOp",EDGE,"E39"),sQuery(id+"F0.wireOp",EDGE,"E40"),sQuery(id+"F0.wireOp",EDGE,"E41"),sQuery(id+"F0.wireOp",EDGE,"E42"),sQuery(id+"F0.wireOp",EDGE,"E43"),sQuery(id+"F0.wireOp",EDGE,"E44"),sQuery(id+"F0.wireOp",EDGE,"E45"),sQuery(id+"F0.wireOp",EDGE,"E46"),sQuery(id+"F0.wireOp",EDGE,"E47"),sQuery(id+"F0.wireOp",EDGE,"E48"),sQuery(id+"F0.wireOp",EDGE,"E49"),sQuery(id+"F0.wireOp",EDGE,"E50"),sQuery(id+"F0.wireOp",EDGE,"E51"),sQuery(id+"F0.wireOp",EDGE,"E52"),sQuery(id+"F0.wireOp",EDGE,"E53"),sQuery(id+"F0.wireOp",EDGE,"E54"),sQuery(id+"F0.wireOp",EDGE,"E55"),sQuery(id+"F0.wireOp",EDGE,"E56"),sQuery(id+"F0.wireOp",EDGE,"E57"),sQuery(id+"F0.wireOp",EDGE,"E58"),sQuery(id+"F0.wireOp",EDGE,"E59"),sQuery(id+"F0.wireOp",EDGE,"E60"),sQuery(id+"F0.wireOp",EDGE,"E61"),sQuery(id+"F0.wireOp",EDGE,"E62"),sQuery(id+"F0.wireOp",EDGE,"E63"),sQuery(id+"F0.wireOp",EDGE,"E64"),sQuery(id+"F0.wireOp",EDGE,"E65"),sQuery(id+"F0.wireOp",EDGE,"E66"),sQuery(id+"F0.wireOp",EDGE,"E67"),sQuery(id+"F0.wireOp",EDGE,"E68"),sQuery(id+"F0.wireOp",EDGE,"E69"),sQuery(id+"F0.wireOp",EDGE,"E70"),sQuery(id+"F0.wireOp",EDGE,"E71"),sQuery(id+"F0.wireOp",EDGE,"E72"),sQuery(id+"F0.wireOp",EDGE,"E73"),sQuery(id+"F0.wireOp",EDGE,"E74"),sQuery(id+"F0.wireOp",EDGE,"E75"),sQuery(id+"F0.wireOp",EDGE,"E76"),sQuery(id+"F0.wireOp",EDGE,"E77"),sQuery(id+"F0.wireOp",EDGE,"E78"),sQuery(id+"F0.wireOp",EDGE,"E79"),sQuery(id+"F0.wireOp",EDGE,"E80")])],"isStart":false});
            var sketch = newSketch(context, id + "F12", { "sketchPlane" : qUnion([Q0])});
            skArc(sketch, "E101", {"start": v(11.29, 11.92) * mm, "mid": v(3.56, 12.77) * mm, "end": v(-4.16, 11.92) * mm});
            skArc(sketch, "E102", {"start": v(19.48, 9.23) * mm, "mid": v(15.54, 11.08) * mm, "end": v(11.29, 11.92) * mm});
            skArc(sketch, "E103", {"start": v(25.2, 5) * mm, "mid": v(22.65, 7.53) * mm, "end": v(19.48, 9.23) * mm});
            skArc(sketch, "E104", {"start": v(29.34, -2.4) * mm, "mid": v(27.77, 1.58) * mm, "end": v(25.2, 5) * mm});
            skLineSegment(sketch, "E105", {"start": v(-4.16, 11.92) * mm, "end": v(29.34, -2.4) * mm});
            skSolve(sketch);
        }
        {
            var Q0;
            Q0 = qSketchRegion(id + "F12", true);
            extrude(context, id + "F13", {"entities" : qUnion([Q0]), "operationType" : NewBodyOperationType.REMOVE, "oppositeDirection" : true, "depth" : 25 * mm});
        }
        {
            var Q0;
            Q0=makeQuery(id+"F1.opExtrude","CAP_FACE",FACE,{"disambiguationData":[OSD([sQuery(id+"F0.wireOp",EDGE,"E0"),sQuery(id+"F0.wireOp",EDGE,"E1"),sQuery(id+"F0.wireOp",EDGE,"E2"),sQuery(id+"F0.wireOp",EDGE,"E3"),sQuery(id+"F0.wireOp",EDGE,"E4"),sQuery(id+"F0.wireOp",EDGE,"E5"),sQuery(id+"F0.wireOp",EDGE,"E6"),sQuery(id+"F0.wireOp",EDGE,"E7"),sQuery(id+"F0.wireOp",EDGE,"E8"),sQuery(id+"F0.wireOp",EDGE,"E9"),sQuery(id+"F0.wireOp",EDGE,"E10"),sQuery(id+"F0.wireOp",EDGE,"E11"),sQuery(id+"F0.wireOp",EDGE,"E12"),sQuery(id+"F0.wireOp",EDGE,"E13"),sQuery(id+"F0.wireOp",EDGE,"E14"),sQuery(id+"F0.wireOp",EDGE,"E15"),sQuery(id+"F0.wireOp",EDGE,"E16"),sQuery(id+"F0.wireOp",EDGE,"E17"),sQuery(id+"F0.wireOp",EDGE,"E18"),sQuery(id+"F0.wireOp",EDGE,"E19"),sQuery(id+"F0.wireOp",EDGE,"E20"),sQuery(id+"F0.wireOp",EDGE,"E21"),sQuery(id+"F0.wireOp",EDGE,"E22"),sQuery(id+"F0.wireOp",EDGE,"E23"),sQuery(id+"F0.wireOp",EDGE,"E24"),sQuery(id+"F0.wireOp",EDGE,"E25"),sQuery(id+"F0.wireOp",EDGE,"E26"),sQuery(id+"F0.wireOp",EDGE,"E27"),sQuery(id+"F0.wireOp",EDGE,"E28"),sQuery(id+"F0.wireOp",EDGE,"E29"),sQuery(id+"F0.wireOp",EDGE,"E30"),sQuery(id+"F0.wireOp",EDGE,"E31"),sQuery(id+"F0.wireOp",EDGE,"E32"),sQuery(id+"F0.wireOp",EDGE,"E33"),sQuery(id+"F0.wireOp",EDGE,"E34"),sQuery(id+"F0.wireOp",EDGE,"E35"),sQuery(id+"F0.wireOp",EDGE,"E36"),sQuery(id+"F0.wireOp",EDGE,"E37"),sQuery(id+"F0.wireOp",EDGE,"E38"),sQuery(id+"F0.wireOp",EDGE,"E39"),sQuery(id+"F0.wireOp",EDGE,"E40"),sQuery(id+"F0.wireOp",EDGE,"E41"),sQuery(id+"F0.wireOp",EDGE,"E42"),sQuery(id+"F0.wireOp",EDGE,"E43"),sQuery(id+"F0.wireOp",EDGE,"E44"),sQuery(id+"F0.wireOp",EDGE,"E45"),sQuery(id+"F0.wireOp",EDGE,"E46"),sQuery(id+"F0.wireOp",EDGE,"E47"),sQuery(id+"F0.wireOp",EDGE,"E48"),sQuery(id+"F0.wireOp",EDGE,"E49"),sQuery(id+"F0.wireOp",EDGE,"E50"),sQuery(id+"F0.wireOp",EDGE,"E51"),sQuery(id+"F0.wireOp",EDGE,"E52"),sQuery(id+"F0.wireOp",EDGE,"E53"),sQuery(id+"F0.wireOp",EDGE,"E54"),sQuery(id+"F0.wireOp",EDGE,"E55"),sQuery(id+"F0.wireOp",EDGE,"E56"),sQuery(id+"F0.wireOp",EDGE,"E57"),sQuery(id+"F0.wireOp",EDGE,"E58"),sQuery(id+"F0.wireOp",EDGE,"E59"),sQuery(id+"F0.wireOp",EDGE,"E60"),sQuery(id+"F0.wireOp",EDGE,"E61"),sQuery(id+"F0.wireOp",EDGE,"E62"),sQuery(id+"F0.wireOp",EDGE,"E63"),sQuery(id+"F0.wireOp",EDGE,"E64"),sQuery(id+"F0.wireOp",EDGE,"E65"),sQuery(id+"F0.wireOp",EDGE,"E66"),sQuery(id+"F0.wireOp",EDGE,"E67"),sQuery(id+"F0.wireOp",EDGE,"E68"),sQuery(id+"F0.wireOp",EDGE,"E69"),sQuery(id+"F0.wireOp",EDGE,"E70"),sQuery(id+"F0.wireOp",EDGE,"E71"),sQuery(id+"F0.wireOp",EDGE,"E72"),sQuery(id+"F0.wireOp",EDGE,"E73"),sQuery(id+"F0.wireOp",EDGE,"E74"),sQuery(id+"F0.wireOp",EDGE,"E75"),sQuery(id+"F0.wireOp",EDGE,"E76"),sQuery(id+"F0.wireOp",EDGE,"E77"),sQuery(id+"F0.wireOp",EDGE,"E78"),sQuery(id+"F0.wireOp",EDGE,"E79"),sQuery(id+"F0.wireOp",EDGE,"E80")])],"isStart":false});
            var sketch = newSketch(context, id + "F14", { "sketchPlane" : qUnion([Q0])});
            skText(sketch, "E106", { "text": "A", "fontName": "OpenSans-Regular.ttf"});
            const initialGuessF14  = {"E106": [0.02555, 0.01318, 1, 0, 0.00909]};
            skSetInitialGuess(sketch, initialGuessF14);
            skSolve(sketch);
        }
        {
            var Q0;
            Q0 = qSketchRegion(id + "F14", true);
            extrude(context, id + "F15", {"entities" : qUnion([Q0]), "operationType" : NewBodyOperationType.REMOVE, "oppositeDirection" : true, "depth" : 25 * mm});
        }
        {
            var Q0;
            {var subQ0=sQuery(id+"F0.wireOp",EDGE,"E80");var subQ1=sQuery(id+"F0.wireOp",EDGE,"E79");var subQ2=sQuery(id+"F0.wireOp",EDGE,"E78");var subQ3=sQuery(id+"F0.wireOp",EDGE,"E77");var subQ4=sQuery(id+"F0.wireOp",EDGE,"E76");var subQ5=sQuery(id+"F0.wireOp",EDGE,"E75");var subQ6=sQuery(id+"F0.wireOp",EDGE,"E74");var subQ7=sQuery(id+"F0.wireOp",EDGE,"E73");var subQ8=sQuery(id+"F0.wireOp",EDGE,"E72");var subQ9=sQuery(id+"F0.wireOp",EDGE,"E71");var subQ10=sQuery(id+"F0.wireOp",EDGE,"E70");var subQ11=sQuery(id+"F0.wireOp",EDGE,"E69");var subQ12=sQuery(id+"F0.wireOp",EDGE,"E68");var subQ13=sQuery(id+"F0.wireOp",EDGE,"E67");var subQ14=sQuery(id+"F0.wireOp",EDGE,"E66");var subQ15=sQuery(id+"F0.wireOp",EDGE,"E65");var subQ16=sQuery(id+"F0.wireOp",EDGE,"E64");var subQ17=sQuery(id+"F0.wireOp",EDGE,"E63");var subQ18=sQuery(id+"F0.wireOp",EDGE,"E62");var subQ19=sQuery(id+"F0.wireOp",EDGE,"E61");var subQ20=sQuery(id+"F0.wireOp",EDGE,"E60");var subQ21=sQuery(id+"F0.wireOp",EDGE,"E59");var subQ22=sQuery(id+"F0.wireOp",EDGE,"E58");var subQ23=sQuery(id+"F0.wireOp",EDGE,"E57");var subQ24=sQuery(id+"F0.wireOp",EDGE,"E56");var subQ25=sQuery(id+"F0.wireOp",EDGE,"E55");var subQ26=sQuery(id+"F0.wireOp",EDGE,"E54");var subQ27=sQuery(id+"F0.wireOp",EDGE,"E53");var subQ28=sQuery(id+"F0.wireOp",EDGE,"E52");var subQ29=sQuery(id+"F0.wireOp",EDGE,"E51");var subQ30=sQuery(id+"F0.wireOp",EDGE,"E50");var subQ31=sQuery(id+"F0.wireOp",EDGE,"E49");var subQ32=sQuery(id+"F0.wireOp",EDGE,"E48");var subQ33=sQuery(id+"F0.wireOp",EDGE,"E47");var subQ34=sQuery(id+"F0.wireOp",EDGE,"E46");var subQ35=sQuery(id+"F0.wireOp",EDGE,"E45");var subQ36=sQuery(id+"F0.wireOp",EDGE,"E44");var subQ37=sQuery(id+"F0.wireOp",EDGE,"E43");var subQ38=sQuery(id+"F0.wireOp",EDGE,"E42");var subQ39=sQuery(id+"F0.wireOp",EDGE,"E41");var subQ40=sQuery(id+"F0.wireOp",EDGE,"E40");var subQ41=sQuery(id+"F0.wireOp",EDGE,"E39");var subQ42=sQuery(id+"F0.wireOp",EDGE,"E38");var subQ43=sQuery(id+"F0.wireOp",EDGE,"E37");var subQ44=sQuery(id+"F0.wireOp",EDGE,"E36");var subQ45=sQuery(id+"F0.wireOp",EDGE,"E35");var subQ46=sQuery(id+"F0.wireOp",EDGE,"E34");var subQ47=sQuery(id+"F0.wireOp",EDGE,"E33");var subQ48=sQuery(id+"F0.wireOp",EDGE,"E32");var subQ49=sQuery(id+"F0.wireOp",EDGE,"E31");var subQ50=sQuery(id+"F0.wireOp",EDGE,"E30");var subQ51=sQuery(id+"F0.wireOp",EDGE,"E29");var subQ52=sQuery(id+"F0.wireOp",EDGE,"E28");var subQ53=sQuery(id+"F0.wireOp",EDGE,"E27");var subQ54=sQuery(id+"F0.wireOp",EDGE,"E26");var subQ55=sQuery(id+"F0.wireOp",EDGE,"E25");var subQ56=sQuery(id+"F0.wireOp",EDGE,"E24");var subQ57=sQuery(id+"F0.wireOp",EDGE,"E23");var subQ58=sQuery(id+"F0.wireOp",EDGE,"E22");var subQ59=sQuery(id+"F0.wireOp",EDGE,"E21");var subQ60=sQuery(id+"F0.wireOp",EDGE,"E20");var subQ61=sQuery(id+"F0.wireOp",EDGE,"E19");var subQ62=sQuery(id+"F0.wireOp",EDGE,"E18");var subQ63=sQuery(id+"F0.wireOp",EDGE,"E17");var subQ64=sQuery(id+"F0.wireOp",EDGE,"E16");var subQ65=sQuery(id+"F0.wireOp",EDGE,"E15");var subQ66=sQuery(id+"F0.wireOp",EDGE,"E14");var subQ67=sQuery(id+"F0.wireOp",EDGE,"E13");var subQ68=sQuery(id+"F0.wireOp",EDGE,"E12");var subQ69=sQuery(id+"F0.wireOp",EDGE,"E11");var subQ70=sQuery(id+"F0.wireOp",EDGE,"E10");var subQ71=sQuery(id+"F0.wireOp",EDGE,"E9");var subQ72=sQuery(id+"F0.wireOp",EDGE,"E8");var subQ73=sQuery(id+"F0.wireOp",EDGE,"E7");var subQ74=sQuery(id+"F0.wireOp",EDGE,"E6");var subQ75=sQuery(id+"F0.wireOp",EDGE,"E5");var subQ76=sQuery(id+"F0.wireOp",EDGE,"E4");var subQ77=sQuery(id+"F0.wireOp",EDGE,"E3");var subQ78=sQuery(id+"F0.wireOp",EDGE,"E2");var subQ79=sQuery(id+"F0.wireOp",EDGE,"E1");var subQ80=sQuery(id+"F0.wireOp",EDGE,"E0");var subQ82=makeQuery(id+"F1.opExtrude","CAP_FACE",FACE,{"disambiguationData":[OSD([subQ80,subQ79,subQ78,subQ77,subQ76,subQ75,subQ74,subQ73,subQ72,subQ71,subQ70,subQ69,subQ68,subQ67,subQ66,subQ65,subQ64,subQ63,subQ62,subQ61,subQ60,subQ59,subQ58,subQ57,subQ56,subQ55,subQ54,subQ53,subQ52,subQ51,subQ50,subQ49,subQ48,subQ47,subQ46,subQ45,subQ44,subQ43,subQ42,subQ41,subQ40,subQ39,subQ38,subQ37,subQ36,subQ35,subQ34,subQ33,subQ32,subQ31,subQ30,subQ29,subQ28,subQ27,subQ26,subQ25,subQ24,subQ23,subQ22,subQ21,subQ20,subQ19,subQ18,subQ17,subQ16,subQ15,subQ14,subQ13,subQ12,subQ11,subQ10,subQ9,subQ8,subQ7,subQ6,subQ5,subQ4,subQ3,subQ2,subQ1,subQ0])],"isStart":false});Q0=makeQuery(id+"F15.boolean.opBoolean","SPLIT",FACE,{"disambiguationData":[TD([makeQuery(id+"F1.opExtrude","SWEPT_FACE",FACE,{"disambiguationData":[OSD([subQ69])]})])],"derivedFrom":subQ82});}
            var sketch = newSketch(context, id + "F16", { "sketchPlane" : qUnion([Q0])});
            skLineSegment(sketch, "E107", {"start": v(27.72, 17.06) * mm, "end": v(28.02, 16.61) * mm});
            skLineSegment(sketch, "E108", {"start": v(28.02, 16.61) * mm, "end": v(31.33, 16.61) * mm});
            skLineSegment(sketch, "E109", {"start": v(31.33, 16.61) * mm, "end": v(31.33, 17.38) * mm});
            skLineSegment(sketch, "E110", {"start": v(31.33, 17.38) * mm, "end": v(29.51, 21.69) * mm});
            skLineSegment(sketch, "E111", {"start": v(29.51, 21.69) * mm, "end": v(27.72, 17.06) * mm});
            skSolve(sketch);
        }
        {
            var Q0;
            Q0 = qSketchRegion(id + "F16", true);
            extrude(context, id + "F17", {"entities" : qUnion([Q0]), "operationType" : NewBodyOperationType.REMOVE, "oppositeDirection" : true, "depth" : 25 * mm});
        }
        {
            var Q0;
            {var subQ0=sQuery(id+"F0.wireOp",EDGE,"E80");var subQ1=sQuery(id+"F0.wireOp",EDGE,"E79");var subQ2=sQuery(id+"F0.wireOp",EDGE,"E78");var subQ3=sQuery(id+"F0.wireOp",EDGE,"E77");var subQ4=sQuery(id+"F0.wireOp",EDGE,"E76");var subQ5=sQuery(id+"F0.wireOp",EDGE,"E75");var subQ6=sQuery(id+"F0.wireOp",EDGE,"E74");var subQ7=sQuery(id+"F0.wireOp",EDGE,"E73");var subQ8=sQuery(id+"F0.wireOp",EDGE,"E72");var subQ9=sQuery(id+"F0.wireOp",EDGE,"E71");var subQ10=sQuery(id+"F0.wireOp",EDGE,"E70");var subQ11=sQuery(id+"F0.wireOp",EDGE,"E69");var subQ12=sQuery(id+"F0.wireOp",EDGE,"E68");var subQ13=sQuery(id+"F0.wireOp",EDGE,"E67");var subQ14=sQuery(id+"F0.wireOp",EDGE,"E66");var subQ15=sQuery(id+"F0.wireOp",EDGE,"E65");var subQ16=sQuery(id+"F0.wireOp",EDGE,"E64");var subQ17=sQuery(id+"F0.wireOp",EDGE,"E63");var subQ18=sQuery(id+"F0.wireOp",EDGE,"E62");var subQ19=sQuery(id+"F0.wireOp",EDGE,"E61");var subQ20=sQuery(id+"F0.wireOp",EDGE,"E60");var subQ21=sQuery(id+"F0.wireOp",EDGE,"E59");var subQ22=sQuery(id+"F0.wireOp",EDGE,"E58");var subQ23=sQuery(id+"F0.wireOp",EDGE,"E57");var subQ24=sQuery(id+"F0.wireOp",EDGE,"E56");var subQ25=sQuery(id+"F0.wireOp",EDGE,"E55");var subQ26=sQuery(id+"F0.wireOp",EDGE,"E54");var subQ27=sQuery(id+"F0.wireOp",EDGE,"E53");var subQ28=sQuery(id+"F0.wireOp",EDGE,"E52");var subQ29=sQuery(id+"F0.wireOp",EDGE,"E51");var subQ30=sQuery(id+"F0.wireOp",EDGE,"E50");var subQ31=sQuery(id+"F0.wireOp",EDGE,"E49");var subQ32=sQuery(id+"F0.wireOp",EDGE,"E48");var subQ33=sQuery(id+"F0.wireOp",EDGE,"E47");var subQ34=sQuery(id+"F0.wireOp",EDGE,"E46");var subQ35=sQuery(id+"F0.wireOp",EDGE,"E45");var subQ36=sQuery(id+"F0.wireOp",EDGE,"E44");var subQ37=sQuery(id+"F0.wireOp",EDGE,"E43");var subQ38=sQuery(id+"F0.wireOp",EDGE,"E42");var subQ39=sQuery(id+"F0.wireOp",EDGE,"E41");var subQ40=sQuery(id+"F0.wireOp",EDGE,"E40");var subQ41=sQuery(id+"F0.wireOp",EDGE,"E39");var subQ42=sQuery(id+"F0.wireOp",EDGE,"E38");var subQ43=sQuery(id+"F0.wireOp",EDGE,"E37");var subQ44=sQuery(id+"F0.wireOp",EDGE,"E36");var subQ45=sQuery(id+"F0.wireOp",EDGE,"E35");var subQ46=sQuery(id+"F0.wireOp",EDGE,"E34");var subQ47=sQuery(id+"F0.wireOp",EDGE,"E33");var subQ48=sQuery(id+"F0.wireOp",EDGE,"E32");var subQ49=sQuery(id+"F0.wireOp",EDGE,"E31");var subQ50=sQuery(id+"F0.wireOp",EDGE,"E30");var subQ51=sQuery(id+"F0.wireOp",EDGE,"E29");var subQ52=sQuery(id+"F0.wireOp",EDGE,"E28");var subQ53=sQuery(id+"F0.wireOp",EDGE,"E27");var subQ54=sQuery(id+"F0.wireOp",EDGE,"E26");var subQ55=sQuery(id+"F0.wireOp",EDGE,"E25");var subQ56=sQuery(id+"F0.wireOp",EDGE,"E24");var subQ57=sQuery(id+"F0.wireOp",EDGE,"E23");var subQ58=sQuery(id+"F0.wireOp",EDGE,"E22");var subQ59=sQuery(id+"F0.wireOp",EDGE,"E21");var subQ60=sQuery(id+"F0.wireOp",EDGE,"E20");var subQ61=sQuery(id+"F0.wireOp",EDGE,"E19");var subQ62=sQuery(id+"F0.wireOp",EDGE,"E18");var subQ63=sQuery(id+"F0.wireOp",EDGE,"E17");var subQ64=sQuery(id+"F0.wireOp",EDGE,"E16");var subQ65=sQuery(id+"F0.wireOp",EDGE,"E15");var subQ66=sQuery(id+"F0.wireOp",EDGE,"E14");var subQ67=sQuery(id+"F0.wireOp",EDGE,"E13");var subQ68=sQuery(id+"F0.wireOp",EDGE,"E12");var subQ69=sQuery(id+"F0.wireOp",EDGE,"E11");var subQ70=sQuery(id+"F0.wireOp",EDGE,"E10");var subQ71=sQuery(id+"F0.wireOp",EDGE,"E9");var subQ72=sQuery(id+"F0.wireOp",EDGE,"E8");var subQ73=sQuery(id+"F0.wireOp",EDGE,"E7");var subQ74=sQuery(id+"F0.wireOp",EDGE,"E6");var subQ75=sQuery(id+"F0.wireOp",EDGE,"E5");var subQ76=sQuery(id+"F0.wireOp",EDGE,"E4");var subQ77=sQuery(id+"F0.wireOp",EDGE,"E3");var subQ78=sQuery(id+"F0.wireOp",EDGE,"E2");var subQ79=sQuery(id+"F0.wireOp",EDGE,"E1");var subQ80=sQuery(id+"F0.wireOp",EDGE,"E0");var subQ81=makeQuery(id+"F1.opExtrude","CAP_FACE",FACE,{"disambiguationData":[OSD([subQ80,subQ79,subQ78,subQ77,subQ76,subQ75,subQ74,subQ73,subQ72,subQ71,subQ70,subQ69,subQ68,subQ67,subQ66,subQ65,subQ64,subQ63,subQ62,subQ61,subQ60,subQ59,subQ58,subQ57,subQ56,subQ55,subQ54,subQ53,subQ52,subQ51,subQ50,subQ49,subQ48,subQ47,subQ46,subQ45,subQ44,subQ43,subQ42,subQ41,subQ40,subQ39,subQ38,subQ37,subQ36,subQ35,subQ34,subQ33,subQ32,subQ31,subQ30,subQ29,subQ28,subQ27,subQ26,subQ25,subQ24,subQ23,subQ22,subQ21,subQ20,subQ19,subQ18,subQ17,subQ16,subQ15,subQ14,subQ13,subQ12,subQ11,subQ10,subQ9,subQ8,subQ7,subQ6,subQ5,subQ4,subQ3,subQ2,subQ1,subQ0])],"isStart":true});Q0=makeQuery(id+"F15.boolean.opBoolean","SPLIT",FACE,{"disambiguationData":[TD([makeQuery(id+"F1.opExtrude","SWEPT_FACE",FACE,{"disambiguationData":[OSD([subQ69])]})])],"derivedFrom":subQ81});}
            var sketch = newSketch(context, id + "F18", { "sketchPlane" : qUnion([Q0])});
            skCircle(sketch, "E112", {"center": v(64.56, -27.58) * mm, "radius": 1.91 * mm});
            skSolve(sketch);
        }
        {
            var Q0;
            Q0 = qSketchRegion(id + "F18", true);
            extrude(context, id + "F19", {"entities" : qUnion([Q0]), "operationType" : NewBodyOperationType.REMOVE, "oppositeDirection" : true, "depth" : 25 * mm});
        }
        {
            var Q0;
            {var subQ0=sQuery(id+"F0.wireOp",EDGE,"E80");var subQ1=sQuery(id+"F0.wireOp",EDGE,"E79");var subQ2=sQuery(id+"F0.wireOp",EDGE,"E78");var subQ3=sQuery(id+"F0.wireOp",EDGE,"E77");var subQ4=sQuery(id+"F0.wireOp",EDGE,"E76");var subQ5=sQuery(id+"F0.wireOp",EDGE,"E75");var subQ6=sQuery(id+"F0.wireOp",EDGE,"E74");var subQ7=sQuery(id+"F0.wireOp",EDGE,"E73");var subQ8=sQuery(id+"F0.wireOp",EDGE,"E72");var subQ9=sQuery(id+"F0.wireOp",EDGE,"E71");var subQ10=sQuery(id+"F0.wireOp",EDGE,"E70");var subQ11=sQuery(id+"F0.wireOp",EDGE,"E69");var subQ12=sQuery(id+"F0.wireOp",EDGE,"E68");var subQ13=sQuery(id+"F0.wireOp",EDGE,"E67");var subQ14=sQuery(id+"F0.wireOp",EDGE,"E66");var subQ15=sQuery(id+"F0.wireOp",EDGE,"E65");var subQ16=sQuery(id+"F0.wireOp",EDGE,"E64");var subQ17=sQuery(id+"F0.wireOp",EDGE,"E63");var subQ18=sQuery(id+"F0.wireOp",EDGE,"E62");var subQ19=sQuery(id+"F0.wireOp",EDGE,"E61");var subQ20=sQuery(id+"F0.wireOp",EDGE,"E60");var subQ21=sQuery(id+"F0.wireOp",EDGE,"E59");var subQ22=sQuery(id+"F0.wireOp",EDGE,"E58");var subQ23=sQuery(id+"F0.wireOp",EDGE,"E57");var subQ24=sQuery(id+"F0.wireOp",EDGE,"E56");var subQ25=sQuery(id+"F0.wireOp",EDGE,"E55");var subQ26=sQuery(id+"F0.wireOp",EDGE,"E54");var subQ27=sQuery(id+"F0.wireOp",EDGE,"E53");var subQ28=sQuery(id+"F0.wireOp",EDGE,"E52");var subQ29=sQuery(id+"F0.wireOp",EDGE,"E51");var subQ30=sQuery(id+"F0.wireOp",EDGE,"E50");var subQ31=sQuery(id+"F0.wireOp",EDGE,"E49");var subQ32=sQuery(id+"F0.wireOp",EDGE,"E48");var subQ33=sQuery(id+"F0.wireOp",EDGE,"E47");var subQ34=sQuery(id+"F0.wireOp",EDGE,"E46");var subQ35=sQuery(id+"F0.wireOp",EDGE,"E45");var subQ36=sQuery(id+"F0.wireOp",EDGE,"E44");var subQ37=sQuery(id+"F0.wireOp",EDGE,"E43");var subQ38=sQuery(id+"F0.wireOp",EDGE,"E42");var subQ39=sQuery(id+"F0.wireOp",EDGE,"E41");var subQ40=sQuery(id+"F0.wireOp",EDGE,"E40");var subQ41=sQuery(id+"F0.wireOp",EDGE,"E39");var subQ42=sQuery(id+"F0.wireOp",EDGE,"E38");var subQ43=sQuery(id+"F0.wireOp",EDGE,"E37");var subQ44=sQuery(id+"F0.wireOp",EDGE,"E36");var subQ45=sQuery(id+"F0.wireOp",EDGE,"E35");var subQ46=sQuery(id+"F0.wireOp",EDGE,"E34");var subQ47=sQuery(id+"F0.wireOp",EDGE,"E33");var subQ48=sQuery(id+"F0.wireOp",EDGE,"E32");var subQ49=sQuery(id+"F0.wireOp",EDGE,"E31");var subQ50=sQuery(id+"F0.wireOp",EDGE,"E30");var subQ51=sQuery(id+"F0.wireOp",EDGE,"E29");var subQ52=sQuery(id+"F0.wireOp",EDGE,"E28");var subQ53=sQuery(id+"F0.wireOp",EDGE,"E27");var subQ54=sQuery(id+"F0.wireOp",EDGE,"E26");var subQ55=sQuery(id+"F0.wireOp",EDGE,"E25");var subQ56=sQuery(id+"F0.wireOp",EDGE,"E24");var subQ57=sQuery(id+"F0.wireOp",EDGE,"E23");var subQ58=sQuery(id+"F0.wireOp",EDGE,"E22");var subQ59=sQuery(id+"F0.wireOp",EDGE,"E21");var subQ60=sQuery(id+"F0.wireOp",EDGE,"E20");var subQ61=sQuery(id+"F0.wireOp",EDGE,"E19");var subQ62=sQuery(id+"F0.wireOp",EDGE,"E18");var subQ63=sQuery(id+"F0.wireOp",EDGE,"E17");var subQ64=sQuery(id+"F0.wireOp",EDGE,"E16");var subQ65=sQuery(id+"F0.wireOp",EDGE,"E15");var subQ66=sQuery(id+"F0.wireOp",EDGE,"E14");var subQ67=sQuery(id+"F0.wireOp",EDGE,"E13");var subQ68=sQuery(id+"F0.wireOp",EDGE,"E12");var subQ69=sQuery(id+"F0.wireOp",EDGE,"E11");var subQ70=sQuery(id+"F0.wireOp",EDGE,"E10");var subQ71=sQuery(id+"F0.wireOp",EDGE,"E9");var subQ72=sQuery(id+"F0.wireOp",EDGE,"E8");var subQ73=sQuery(id+"F0.wireOp",EDGE,"E7");var subQ74=sQuery(id+"F0.wireOp",EDGE,"E6");var subQ75=sQuery(id+"F0.wireOp",EDGE,"E5");var subQ76=sQuery(id+"F0.wireOp",EDGE,"E4");var subQ77=sQuery(id+"F0.wireOp",EDGE,"E3");var subQ78=sQuery(id+"F0.wireOp",EDGE,"E2");var subQ79=sQuery(id+"F0.wireOp",EDGE,"E1");var subQ80=sQuery(id+"F0.wireOp",EDGE,"E0");var subQ82=makeQuery(id+"F1.opExtrude","CAP_FACE",FACE,{"disambiguationData":[OSD([subQ80,subQ79,subQ78,subQ77,subQ76,subQ75,subQ74,subQ73,subQ72,subQ71,subQ70,subQ69,subQ68,subQ67,subQ66,subQ65,subQ64,subQ63,subQ62,subQ61,subQ60,subQ59,subQ58,subQ57,subQ56,subQ55,subQ54,subQ53,subQ52,subQ51,subQ50,subQ49,subQ48,subQ47,subQ46,subQ45,subQ44,subQ43,subQ42,subQ41,subQ40,subQ39,subQ38,subQ37,subQ36,subQ35,subQ34,subQ33,subQ32,subQ31,subQ30,subQ29,subQ28,subQ27,subQ26,subQ25,subQ24,subQ23,subQ22,subQ21,subQ20,subQ19,subQ18,subQ17,subQ16,subQ15,subQ14,subQ13,subQ12,subQ11,subQ10,subQ9,subQ8,subQ7,subQ6,subQ5,subQ4,subQ3,subQ2,subQ1,subQ0])],"isStart":false});Q0=makeQuery(id+"F15.boolean.opBoolean","SPLIT",FACE,{"disambiguationData":[TD([makeQuery(id+"F1.opExtrude","SWEPT_FACE",FACE,{"disambiguationData":[OSD([subQ69])]})])],"derivedFrom":subQ82});}
            var sketch = newSketch(context, id + "F20", { "sketchPlane" : qUnion([Q0])});
            skText(sketch, "E113", { "text": "Ariza", "fontName": "OpenSans-Regular.ttf"});
            const initialGuessF20  = {"E113": [0.02345, 0.0089, 1, 0, 0.00359]};
            skSetInitialGuess(sketch, initialGuessF20);
            skSolve(sketch);
        }
        {
            var Q0;
            Q0 = qSketchRegion(id + "F20", true);
            extrude(context, id + "F21", {"entities" : qUnion([Q0]), "operationType" : NewBodyOperationType.REMOVE, "oppositeDirection" : true, "depth" : 25 * mm});
        }
        {
            var Q0;
            {var subQ1=sQuery(id+"F0.wireOp",EDGE,"E80");var subQ2=sQuery(id+"F0.wireOp",EDGE,"E79");var subQ3=sQuery(id+"F0.wireOp",EDGE,"E78");var subQ4=sQuery(id+"F0.wireOp",EDGE,"E77");var subQ5=sQuery(id+"F0.wireOp",EDGE,"E76");var subQ6=sQuery(id+"F0.wireOp",EDGE,"E75");var subQ7=sQuery(id+"F0.wireOp",EDGE,"E74");var subQ8=sQuery(id+"F0.wireOp",EDGE,"E73");var subQ9=sQuery(id+"F0.wireOp",EDGE,"E72");var subQ10=sQuery(id+"F0.wireOp",EDGE,"E71");var subQ11=sQuery(id+"F0.wireOp",EDGE,"E70");var subQ12=sQuery(id+"F0.wireOp",EDGE,"E69");var subQ13=sQuery(id+"F0.wireOp",EDGE,"E68");var subQ14=sQuery(id+"F0.wireOp",EDGE,"E67");var subQ15=sQuery(id+"F0.wireOp",EDGE,"E66");var subQ16=sQuery(id+"F0.wireOp",EDGE,"E65");var subQ17=sQuery(id+"F0.wireOp",EDGE,"E64");var subQ18=sQuery(id+"F0.wireOp",EDGE,"E63");var subQ19=sQuery(id+"F0.wireOp",EDGE,"E62");var subQ20=sQuery(id+"F0.wireOp",EDGE,"E61");var subQ21=sQuery(id+"F0.wireOp",EDGE,"E60");var subQ22=sQuery(id+"F0.wireOp",EDGE,"E59");var subQ23=sQuery(id+"F0.wireOp",EDGE,"E58");var subQ24=sQuery(id+"F0.wireOp",EDGE,"E57");var subQ25=sQuery(id+"F0.wireOp",EDGE,"E56");var subQ26=sQuery(id+"F0.wireOp",EDGE,"E55");var subQ27=sQuery(id+"F0.wireOp",EDGE,"E54");var subQ28=sQuery(id+"F0.wireOp",EDGE,"E53");var subQ29=sQuery(id+"F0.wireOp",EDGE,"E52");var subQ30=sQuery(id+"F0.wireOp",EDGE,"E51");var subQ31=sQuery(id+"F0.wireOp",EDGE,"E50");var subQ32=sQuery(id+"F0.wireOp",EDGE,"E49");var subQ33=sQuery(id+"F0.wireOp",EDGE,"E48");var subQ34=sQuery(id+"F0.wireOp",EDGE,"E47");var subQ35=sQuery(id+"F0.wireOp",EDGE,"E46");var subQ36=sQuery(id+"F0.wireOp",EDGE,"E45");var subQ37=sQuery(id+"F0.wireOp",EDGE,"E44");var subQ38=sQuery(id+"F0.wireOp",EDGE,"E43");var subQ39=sQuery(id+"F0.wireOp",EDGE,"E42");var subQ40=sQuery(id+"F0.wireOp",EDGE,"E41");var subQ41=sQuery(id+"F0.wireOp",EDGE,"E40");var subQ42=sQuery(id+"F0.wireOp",EDGE,"E39");var subQ43=sQuery(id+"F0.wireOp",EDGE,"E38");var subQ44=sQuery(id+"F0.wireOp",EDGE,"E37");var subQ45=sQuery(id+"F0.wireOp",EDGE,"E36");var subQ46=sQuery(id+"F0.wireOp",EDGE,"E35");var subQ47=sQuery(id+"F0.wireOp",EDGE,"E34");var subQ48=sQuery(id+"F0.wireOp",EDGE,"E33");var subQ49=sQuery(id+"F0.wireOp",EDGE,"E32");var subQ50=sQuery(id+"F0.wireOp",EDGE,"E31");var subQ51=sQuery(id+"F0.wireOp",EDGE,"E30");var subQ52=sQuery(id+"F0.wireOp",EDGE,"E29");var subQ53=sQuery(id+"F0.wireOp",EDGE,"E28");var subQ54=sQuery(id+"F0.wireOp",EDGE,"E27");var subQ55=sQuery(id+"F0.wireOp",EDGE,"E26");var subQ56=sQuery(id+"F0.wireOp",EDGE,"E25");var subQ57=sQuery(id+"F0.wireOp",EDGE,"E24");var subQ58=sQuery(id+"F0.wireOp",EDGE,"E23");var subQ59=sQuery(id+"F0.wireOp",EDGE,"E22");var subQ60=sQuery(id+"F0.wireOp",EDGE,"E21");var subQ61=sQuery(id+"F0.wireOp",EDGE,"E20");var subQ62=sQuery(id+"F0.wireOp",EDGE,"E19");var subQ63=sQuery(id+"F0.wireOp",EDGE,"E18");var subQ64=sQuery(id+"F0.wireOp",EDGE,"E17");var subQ65=sQuery(id+"F0.wireOp",EDGE,"E16");var subQ66=sQuery(id+"F0.wireOp",EDGE,"E15");var subQ67=sQuery(id+"F0.wireOp",EDGE,"E14");var subQ68=sQuery(id+"F0.wireOp",EDGE,"E13");var subQ69=sQuery(id+"F0.wireOp",EDGE,"E12");var subQ70=sQuery(id+"F0.wireOp",EDGE,"E11");var subQ71=sQuery(id+"F0.wireOp",EDGE,"E10");var subQ72=sQuery(id+"F0.wireOp",EDGE,"E9");var subQ73=sQuery(id+"F0.wireOp",EDGE,"E8");var subQ74=sQuery(id+"F0.wireOp",EDGE,"E7");var subQ75=sQuery(id+"F0.wireOp",EDGE,"E6");var subQ76=sQuery(id+"F0.wireOp",EDGE,"E5");var subQ77=sQuery(id+"F0.wireOp",EDGE,"E4");var subQ78=sQuery(id+"F0.wireOp",EDGE,"E3");var subQ79=sQuery(id+"F0.wireOp",EDGE,"E2");var subQ80=sQuery(id+"F0.wireOp",EDGE,"E1");var subQ81=sQuery(id+"F0.wireOp",EDGE,"E0");var subQ84=makeQuery(id+"F1.opExtrude","CAP_FACE",FACE,{"disambiguationData":[OSD([subQ81,subQ80,subQ79,subQ78,subQ77,subQ76,subQ75,subQ74,subQ73,subQ72,subQ71,subQ70,subQ69,subQ68,subQ67,subQ66,subQ65,subQ64,subQ63,subQ62,subQ61,subQ60,subQ59,subQ58,subQ57,subQ56,subQ55,subQ54,subQ53,subQ52,subQ51,subQ50,subQ49,subQ48,subQ47,subQ46,subQ45,subQ44,subQ43,subQ42,subQ41,subQ40,subQ39,subQ38,subQ37,subQ36,subQ35,subQ34,subQ33,subQ32,subQ31,subQ30,subQ29,subQ28,subQ27,subQ26,subQ25,subQ24,subQ23,subQ22,subQ21,subQ20,subQ19,subQ18,subQ17,subQ16,subQ15,subQ14,subQ13,subQ12,subQ11,subQ10,subQ9,subQ8,subQ7,subQ6,subQ5,subQ4,subQ3,subQ2,subQ1])],"isStart":false});var subQ118=makeQuery(id+"F1.opExtrude","SWEPT_FACE",FACE,{"disambiguationData":[OSD([subQ70])]});Q0=makeQuery(id+"F21.boolean.opBoolean","SPLIT",FACE,{"disambiguationData":[TD([subQ118])],"derivedFrom":makeQuery(id+"F15.boolean.opBoolean","SPLIT",FACE,{"disambiguationData":[TD([subQ118])],"derivedFrom":subQ84})});}
            var sketch = newSketch(context, id + "F22", { "sketchPlane" : qUnion([Q0])});
            skLineSegment(sketch, "E114", {"start": v(25.1, 12.24) * mm, "end": v(24.89, 12.16) * mm});
            skLineSegment(sketch, "E115", {"start": v(24.89, 12.16) * mm, "end": v(24.22, 10.24) * mm});
            skLineSegment(sketch, "E116", {"start": v(24.22, 10.24) * mm, "end": v(25.86, 10.24) * mm});
            skLineSegment(sketch, "E117", {"start": v(25.86, 10.24) * mm, "end": v(25.1, 12.24) * mm});
            skSolve(sketch);
        }
        {
            var Q0;
            Q0 = qSketchRegion(id + "F22", true);
            extrude(context, id + "F23", {"entities" : qUnion([Q0]), "operationType" : NewBodyOperationType.REMOVE, "oppositeDirection" : true, "depth" : 25 * mm});
        }
        {
            var Q0;
            {var subQ1=sQuery(id+"F0.wireOp",EDGE,"E80");var subQ2=sQuery(id+"F0.wireOp",EDGE,"E79");var subQ3=sQuery(id+"F0.wireOp",EDGE,"E78");var subQ4=sQuery(id+"F0.wireOp",EDGE,"E77");var subQ5=sQuery(id+"F0.wireOp",EDGE,"E76");var subQ6=sQuery(id+"F0.wireOp",EDGE,"E75");var subQ7=sQuery(id+"F0.wireOp",EDGE,"E74");var subQ8=sQuery(id+"F0.wireOp",EDGE,"E73");var subQ9=sQuery(id+"F0.wireOp",EDGE,"E72");var subQ10=sQuery(id+"F0.wireOp",EDGE,"E71");var subQ11=sQuery(id+"F0.wireOp",EDGE,"E70");var subQ12=sQuery(id+"F0.wireOp",EDGE,"E69");var subQ13=sQuery(id+"F0.wireOp",EDGE,"E68");var subQ14=sQuery(id+"F0.wireOp",EDGE,"E67");var subQ15=sQuery(id+"F0.wireOp",EDGE,"E66");var subQ16=sQuery(id+"F0.wireOp",EDGE,"E65");var subQ17=sQuery(id+"F0.wireOp",EDGE,"E64");var subQ18=sQuery(id+"F0.wireOp",EDGE,"E63");var subQ19=sQuery(id+"F0.wireOp",EDGE,"E62");var subQ20=sQuery(id+"F0.wireOp",EDGE,"E61");var subQ21=sQuery(id+"F0.wireOp",EDGE,"E60");var subQ22=sQuery(id+"F0.wireOp",EDGE,"E59");var subQ23=sQuery(id+"F0.wireOp",EDGE,"E58");var subQ24=sQuery(id+"F0.wireOp",EDGE,"E57");var subQ25=sQuery(id+"F0.wireOp",EDGE,"E56");var subQ26=sQuery(id+"F0.wireOp",EDGE,"E55");var subQ27=sQuery(id+"F0.wireOp",EDGE,"E54");var subQ28=sQuery(id+"F0.wireOp",EDGE,"E53");var subQ29=sQuery(id+"F0.wireOp",EDGE,"E52");var subQ30=sQuery(id+"F0.wireOp",EDGE,"E51");var subQ31=sQuery(id+"F0.wireOp",EDGE,"E50");var subQ32=sQuery(id+"F0.wireOp",EDGE,"E49");var subQ33=sQuery(id+"F0.wireOp",EDGE,"E48");var subQ34=sQuery(id+"F0.wireOp",EDGE,"E47");var subQ35=sQuery(id+"F0.wireOp",EDGE,"E46");var subQ36=sQuery(id+"F0.wireOp",EDGE,"E45");var subQ37=sQuery(id+"F0.wireOp",EDGE,"E44");var subQ38=sQuery(id+"F0.wireOp",EDGE,"E43");var subQ39=sQuery(id+"F0.wireOp",EDGE,"E42");var subQ40=sQuery(id+"F0.wireOp",EDGE,"E41");var subQ41=sQuery(id+"F0.wireOp",EDGE,"E40");var subQ42=sQuery(id+"F0.wireOp",EDGE,"E39");var subQ43=sQuery(id+"F0.wireOp",EDGE,"E38");var subQ44=sQuery(id+"F0.wireOp",EDGE,"E37");var subQ45=sQuery(id+"F0.wireOp",EDGE,"E36");var subQ46=sQuery(id+"F0.wireOp",EDGE,"E35");var subQ47=sQuery(id+"F0.wireOp",EDGE,"E34");var subQ48=sQuery(id+"F0.wireOp",EDGE,"E33");var subQ49=sQuery(id+"F0.wireOp",EDGE,"E32");var subQ50=sQuery(id+"F0.wireOp",EDGE,"E31");var subQ51=sQuery(id+"F0.wireOp",EDGE,"E30");var subQ52=sQuery(id+"F0.wireOp",EDGE,"E29");var subQ53=sQuery(id+"F0.wireOp",EDGE,"E28");var subQ54=sQuery(id+"F0.wireOp",EDGE,"E27");var subQ55=sQuery(id+"F0.wireOp",EDGE,"E26");var subQ56=sQuery(id+"F0.wireOp",EDGE,"E25");var subQ57=sQuery(id+"F0.wireOp",EDGE,"E24");var subQ58=sQuery(id+"F0.wireOp",EDGE,"E23");var subQ59=sQuery(id+"F0.wireOp",EDGE,"E22");var subQ60=sQuery(id+"F0.wireOp",EDGE,"E21");var subQ61=sQuery(id+"F0.wireOp",EDGE,"E20");var subQ62=sQuery(id+"F0.wireOp",EDGE,"E19");var subQ63=sQuery(id+"F0.wireOp",EDGE,"E18");var subQ64=sQuery(id+"F0.wireOp",EDGE,"E17");var subQ65=sQuery(id+"F0.wireOp",EDGE,"E16");var subQ66=sQuery(id+"F0.wireOp",EDGE,"E15");var subQ67=sQuery(id+"F0.wireOp",EDGE,"E14");var subQ68=sQuery(id+"F0.wireOp",EDGE,"E13");var subQ69=sQuery(id+"F0.wireOp",EDGE,"E12");var subQ70=sQuery(id+"F0.wireOp",EDGE,"E11");var subQ71=sQuery(id+"F0.wireOp",EDGE,"E10");var subQ72=sQuery(id+"F0.wireOp",EDGE,"E9");var subQ73=sQuery(id+"F0.wireOp",EDGE,"E8");var subQ74=sQuery(id+"F0.wireOp",EDGE,"E7");var subQ75=sQuery(id+"F0.wireOp",EDGE,"E6");var subQ76=sQuery(id+"F0.wireOp",EDGE,"E5");var subQ77=sQuery(id+"F0.wireOp",EDGE,"E4");var subQ78=sQuery(id+"F0.wireOp",EDGE,"E3");var subQ79=sQuery(id+"F0.wireOp",EDGE,"E2");var subQ80=sQuery(id+"F0.wireOp",EDGE,"E1");var subQ81=sQuery(id+"F0.wireOp",EDGE,"E0");var subQ84=makeQuery(id+"F1.opExtrude","CAP_FACE",FACE,{"disambiguationData":[OSD([subQ81,subQ80,subQ79,subQ78,subQ77,subQ76,subQ75,subQ74,subQ73,subQ72,subQ71,subQ70,subQ69,subQ68,subQ67,subQ66,subQ65,subQ64,subQ63,subQ62,subQ61,subQ60,subQ59,subQ58,subQ57,subQ56,subQ55,subQ54,subQ53,subQ52,subQ51,subQ50,subQ49,subQ48,subQ47,subQ46,subQ45,subQ44,subQ43,subQ42,subQ41,subQ40,subQ39,subQ38,subQ37,subQ36,subQ35,subQ34,subQ33,subQ32,subQ31,subQ30,subQ29,subQ28,subQ27,subQ26,subQ25,subQ24,subQ23,subQ22,subQ21,subQ20,subQ19,subQ18,subQ17,subQ16,subQ15,subQ14,subQ13,subQ12,subQ11,subQ10,subQ9,subQ8,subQ7,subQ6,subQ5,subQ4,subQ3,subQ2,subQ1])],"isStart":false});var subQ118=makeQuery(id+"F1.opExtrude","SWEPT_FACE",FACE,{"disambiguationData":[OSD([subQ70])]});Q0=makeQuery(id+"F21.boolean.opBoolean","SPLIT",FACE,{"disambiguationData":[TD([subQ118])],"derivedFrom":makeQuery(id+"F15.boolean.opBoolean","SPLIT",FACE,{"disambiguationData":[TD([subQ118])],"derivedFrom":subQ84})});}
            var sketch = newSketch(context, id + "F24", { "sketchPlane" : qUnion([Q0])});
            skLineSegment(sketch, "E118", {"start": v(34.2, 10.37) * mm, "end": v(32.83, 10.18) * mm});
            skLineSegment(sketch, "E119", {"start": v(32.83, 10.18) * mm, "end": v(32.83, 9.17) * mm});
            skLineSegment(sketch, "E120", {"start": v(32.83, 9.17) * mm, "end": v(33.75, 9.03) * mm});
            skLineSegment(sketch, "E121", {"start": v(33.75, 9.03) * mm, "end": v(34.37, 9.64) * mm});
            skLineSegment(sketch, "E122", {"start": v(34.37, 9.64) * mm, "end": v(34.2, 10.37) * mm});
            skSolve(sketch);
        }
        {
            var Q0;
            Q0 = qSketchRegion(id + "F24", true);
            extrude(context, id + "F25", {"entities" : qUnion([Q0]), "operationType" : NewBodyOperationType.REMOVE, "oppositeDirection" : true, "depth" : 25 * mm});
        }
    });
